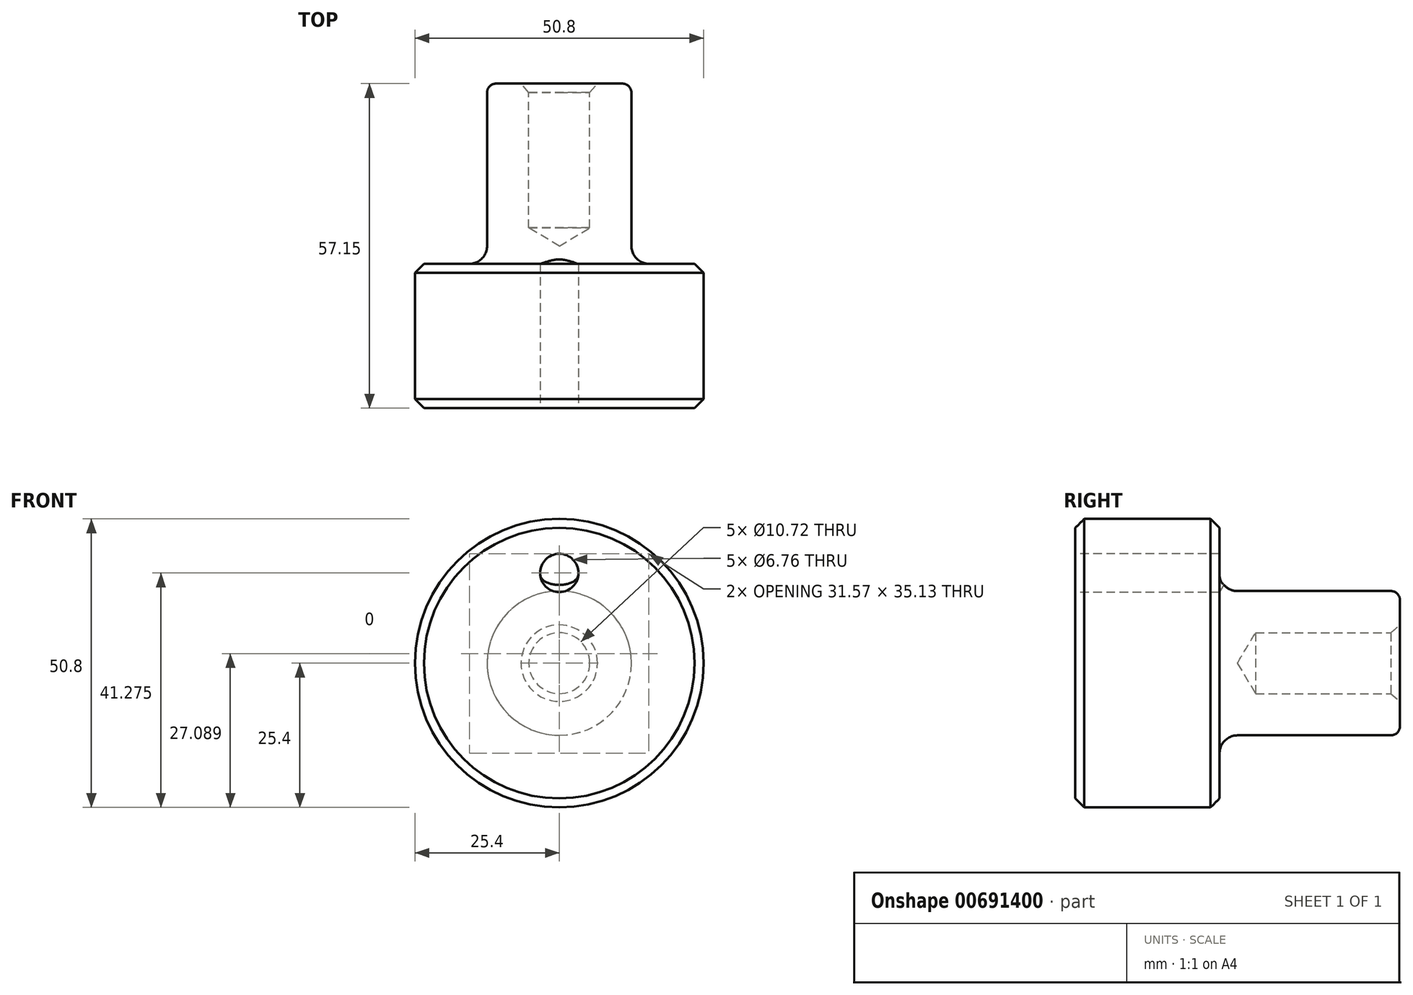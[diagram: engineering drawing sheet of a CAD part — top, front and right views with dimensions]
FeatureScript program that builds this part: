
annotation { "Feature Type Name" : "Feature", "Feature Type Description" : "" }
export const myFeature = defineFeature(function(context is Context, id is Id, definition is map)
    precondition{}
    {
        {
            var Q0;
            Q0=qCreatedBy(makeId("Right.planeOp"),FACE);
            var sketch = newSketch(context, id + "F0", { "sketchPlane" : qUnion([Q0])});
            skLineSegment(sketch, "E0", {"start": v(0, 0) * mm, "end": v(0, 25.4) * mm});
            skLineSegment(sketch, "E1", {"start": v(0, 25.4) * mm, "end": v(25.4, 25.4) * mm});
            skLineSegment(sketch, "E2", {"start": v(25.4, 25.4) * mm, "end": v(25.4, 15.88) * mm});
            skLineSegment(sketch, "E3", {"start": v(28.58, 12.7) * mm, "end": v(57.15, 12.7) * mm});
            skLineSegment(sketch, "E4", {"start": v(57.15, 12.7) * mm, "end": v(57.15, 0) * mm});
            skLineSegment(sketch, "E5", {"start": v(57.15, 0) * mm, "end": v(0, 0) * mm});
            skPoint(sketch, "E6.visualSharp", {"position": v(25.4, 12.7) * mm});
            skArc(sketch, "E6.filletArc", {"start": v(25.4, 15.88) * mm, "mid": v(26.33, 13.63) * mm, "end": v(28.58, 12.7) * mm});
            skSolve(sketch);
        }
        {
            var Q0;
            Q0=makeQuery(id+"F0.imprint","IMPRINT",FACE,{"disambiguationData":[TD([[makeQuery(id+"F0.imprint","IMPRINT",EDGE,{"derivedFrom":sQuery(id+"F0.wireOp",EDGE,"E0")}),-1.0]])]});
            var Q1;
            Q1=sQuery(id+"F0.wireOp",EDGE,"E5");
            revolve(context, id + "F1", {"entities" : qUnion([Q0]), "axis" : qUnion([Q1]), "revolveType" : RevolveType.FULL});
        }
        {
            var Q0;
            Q0=makeQuery(id+"F1.opRevolve","SWEPT_FACE",FACE,{"disambiguationData":[OSD([sQuery(id+"F0.wireOp",EDGE,"E1")])]});
            chamfer(context, id + "F2", {"entities" : qUnion([Q0]), "width" : 1.59 * mm, "tangentPropagation" : true});
        }
        {
            var Q0;
            Q0=makeQuery(id+"F1.opRevolve","SWEPT_FACE",FACE,{"disambiguationData":[OSD([sQuery(id+"F0.wireOp",EDGE,"E4")])]});
            var sketch = newSketch(context, id + "F3", { "sketchPlane" : qUnion([Q0])});
            skPoint(sketch, "E7", {"position": v(0, 0) * mm});
            skSolve(sketch);
        }
        {
            var Q0;
            Q0=sQuery(id+"F3.wireOp",VERTEX,"E7");
            var Q1;
            Q1=makeQuery(id+"F1.opRevolve","SWEPT_BODY",BODY,{"disambiguationData":[OSD([sQuery(id+"F0.wireOp",EDGE,"E0"),sQuery(id+"F0.wireOp",EDGE,"E1"),sQuery(id+"F0.wireOp",EDGE,"E2"),sQuery(id+"F0.wireOp",EDGE,"E3"),sQuery(id+"F0.wireOp",EDGE,"E4"),sQuery(id+"F0.wireOp",EDGE,"E5"),sQuery(id+"F0.wireOp",EDGE,"E6.filletArc")])]});
            hole(context, id + "F4", {"style" : HoleStyle.C_SINK, "endStyle" : HoleEndStyle.BLIND, "holeDiameter" : 10.72 * mm, "cSinkDiameter" : 13.46 * mm, "cSinkAngle" : 82 * degree, "majorDiameter" : 12.7 * mm, "holeDepth" : 25.4 * mm, "isTappedThrough" : true, "tappedDepth" : 19.54 * mm, "tapClearance" : 3, "startFromSketch" : true, "locations" : qUnion([Q0]), "scope" : qUnion([Q1])});
        }
        {
            var Q0;
            Q0=makeQuery(id+"F1.opRevolve","SWEPT_EDGE",EDGE,{"disambiguationData":[OSD([sQuery(id+"F0.wireOp",EDGE,"E3"),sQuery(id+"F0.wireOp",EDGE,"E4")])]});
            fillet(context, id + "F5", {"entities" : qUnion([Q0]), "radius" : 1.59 * mm, "tangentPropagation" : true, "allowEdgeOverflow" : false});
        }
        {
            var Q0;
            Q0=makeQuery(id+"F1.opRevolve","SWEPT_FACE",FACE,{"disambiguationData":[OSD([sQuery(id+"F0.wireOp",EDGE,"E0")])]});
            var sketch = newSketch(context, id + "F6", { "sketchPlane" : qUnion([Q0])});
            skCircle(sketch, "E8", {"center": v(0, 0) * mm, "radius": 15.88 * mm});
            skLineSegment(sketch, "E9", {"start": v(0, 0) * mm, "end": v(0, 15.88) * mm});
            skPoint(sketch, "E10", {"position": v(0, 15.88) * mm});
            skSolve(sketch);
        }
        {
            var Q0;
            Q0=sQuery(id+"F6.wireOp",VERTEX,"E10");
            var Q1;
            Q1=makeQuery(id+"F1.opRevolve","SWEPT_BODY",BODY,{"disambiguationData":[OSD([sQuery(id+"F0.wireOp",EDGE,"E0"),sQuery(id+"F0.wireOp",EDGE,"E1"),sQuery(id+"F0.wireOp",EDGE,"E2"),sQuery(id+"F0.wireOp",EDGE,"E3"),sQuery(id+"F0.wireOp",EDGE,"E4"),sQuery(id+"F0.wireOp",EDGE,"E5"),sQuery(id+"F0.wireOp",EDGE,"E6.filletArc")])]});
            hole(context, id + "F7", {"style" : HoleStyle.SIMPLE, "endStyle" : HoleEndStyle.BLIND, "standardTappedOrClearance" : lookupTablePath({ "standard" : "ANSI", "fit" : "Normal (ASME)", "size" : "1/4", "type" : "Clearance" }), "standardBlindInLast" : lookupTablePath({ "fit" : "Free", "standard" : "ANSI", "size" : "1/4", "type" : "Clearance" }), "holeDiameter" : 6.76 * mm, "majorDiameter" : 6.35 * mm, "holeDepth" : 25.4 * mm, "isTappedThrough" : true, "tappedDepth" : 19.53 * mm, "tapClearance" : 3, "startFromSketch" : true, "locations" : qUnion([Q0]), "scope" : qUnion([Q1])});
        }
    });
